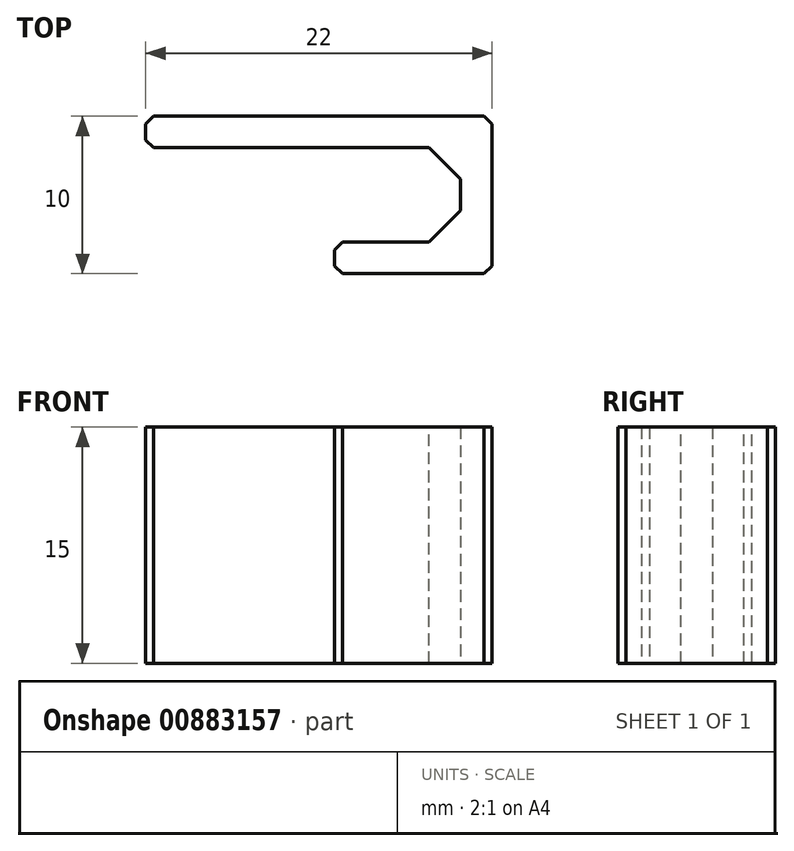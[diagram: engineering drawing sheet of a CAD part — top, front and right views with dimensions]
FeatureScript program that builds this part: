
annotation { "Feature Type Name" : "Feature", "Feature Type Description" : "" }
export const myFeature = defineFeature(function(context is Context, id is Id, definition is map)
    precondition{}
    {
        {
            var Q0;
            Q0=qCreatedBy(makeId("Top.planeOp"),FACE);
            var sketch = newSketch(context, id + "F0", { "sketchPlane" : qUnion([Q0])});
            skLineSegment(sketch, "E0", {"start": v(0, 0) * mm, "end": v(20, 0) * mm});
            skLineSegment(sketch, "E1", {"start": v(20, 0) * mm, "end": v(20, -6) * mm});
            skLineSegment(sketch, "E2", {"start": v(20, -6) * mm, "end": v(12, -6) * mm});
            skLineSegment(sketch, "E3.0", {"start": v(0, 2) * mm, "end": v(20, 2) * mm});
            skLineSegment(sketch, "E4.0", {"start": v(22, 0) * mm, "end": v(22, -6) * mm});
            skLineSegment(sketch, "E5.0", {"start": v(20, -8) * mm, "end": v(12, -8) * mm});
            skLineSegment(sketch, "E6", {"start": v(0, 2) * mm, "end": v(0, 0) * mm});
            skLineSegment(sketch, "E7", {"start": v(20, 2) * mm, "end": v(22, 2) * mm});
            skLineSegment(sketch, "E8", {"start": v(22, 2) * mm, "end": v(22, 0) * mm});
            skLineSegment(sketch, "E9", {"start": v(22, -6) * mm, "end": v(22, -8) * mm});
            skLineSegment(sketch, "E10", {"start": v(22, -8) * mm, "end": v(20, -8) * mm});
            skLineSegment(sketch, "E11", {"start": v(12, -8) * mm, "end": v(12, -6) * mm});
            skSolve(sketch);
        }
        {
            var Q0;
            Q0=makeQuery(id+"F0.imprint","IMPRINT",FACE,{"disambiguationData":[TD([[makeQuery(id+"F0.imprint","IMPRINT",EDGE,{"derivedFrom":sQuery(id+"F0.wireOp",EDGE,"E0")}),1.0]])]});
            extrude(context, id + "F1", {"entities" : qUnion([Q0]), "depth" : 15 * mm, "offsetDistance" : 25 * mm});
        }
        {
            var Q0;
            Q0=makeQuery(id+"F1.opExtrude","SWEPT_EDGE",EDGE,{"disambiguationData":[OSD([sQuery(id+"F0.wireOp",EDGE,"E3.0"),sQuery(id+"F0.wireOp",EDGE,"E6")])]});
            var Q1;
            Q1=makeQuery(id+"F1.opExtrude","SWEPT_EDGE",EDGE,{"disambiguationData":[OSD([sQuery(id+"F0.wireOp",EDGE,"E0"),sQuery(id+"F0.wireOp",EDGE,"E6")])]});
            var Q2;
            Q2=makeQuery(id+"F1.opExtrude","SWEPT_EDGE",EDGE,{"disambiguationData":[OSD([sQuery(id+"F0.wireOp",EDGE,"E5.0"),sQuery(id+"F0.wireOp",EDGE,"E11")])]});
            var Q3;
            Q3=makeQuery(id+"F1.opExtrude","SWEPT_EDGE",EDGE,{"disambiguationData":[OSD([sQuery(id+"F0.wireOp",EDGE,"E2"),sQuery(id+"F0.wireOp",EDGE,"E11")])]});
            var Q4;
            Q4=makeQuery(id+"F1.opExtrude","SWEPT_EDGE",EDGE,{"disambiguationData":[OSD([sQuery(id+"F0.wireOp",EDGE,"E9"),sQuery(id+"F0.wireOp",EDGE,"E10")])]});
            var Q5;
            Q5=makeQuery(id+"F1.opExtrude","SWEPT_EDGE",EDGE,{"disambiguationData":[OSD([sQuery(id+"F0.wireOp",EDGE,"E7"),sQuery(id+"F0.wireOp",EDGE,"E8")])]});
            chamfer(context, id + "F2", {"entities" : qUnion([Q0, Q1, Q2, Q3, Q4, Q5]), "width" : .5 * mm, "tangentPropagation" : true});
        }
        {
            var Q0;
            Q0=makeQuery(id+"F1.opExtrude","SWEPT_EDGE",EDGE,{"disambiguationData":[OSD([sQuery(id+"F0.wireOp",EDGE,"E0"),sQuery(id+"F0.wireOp",EDGE,"E1")])]});
            var Q1;
            Q1=makeQuery(id+"F1.opExtrude","SWEPT_EDGE",EDGE,{"disambiguationData":[OSD([sQuery(id+"F0.wireOp",EDGE,"E1"),sQuery(id+"F0.wireOp",EDGE,"E2")])]});
            chamfer(context, id + "F3", {"entities" : qUnion([Q0, Q1]), "width" : 2 * mm, "tangentPropagation" : true});
        }
    });
